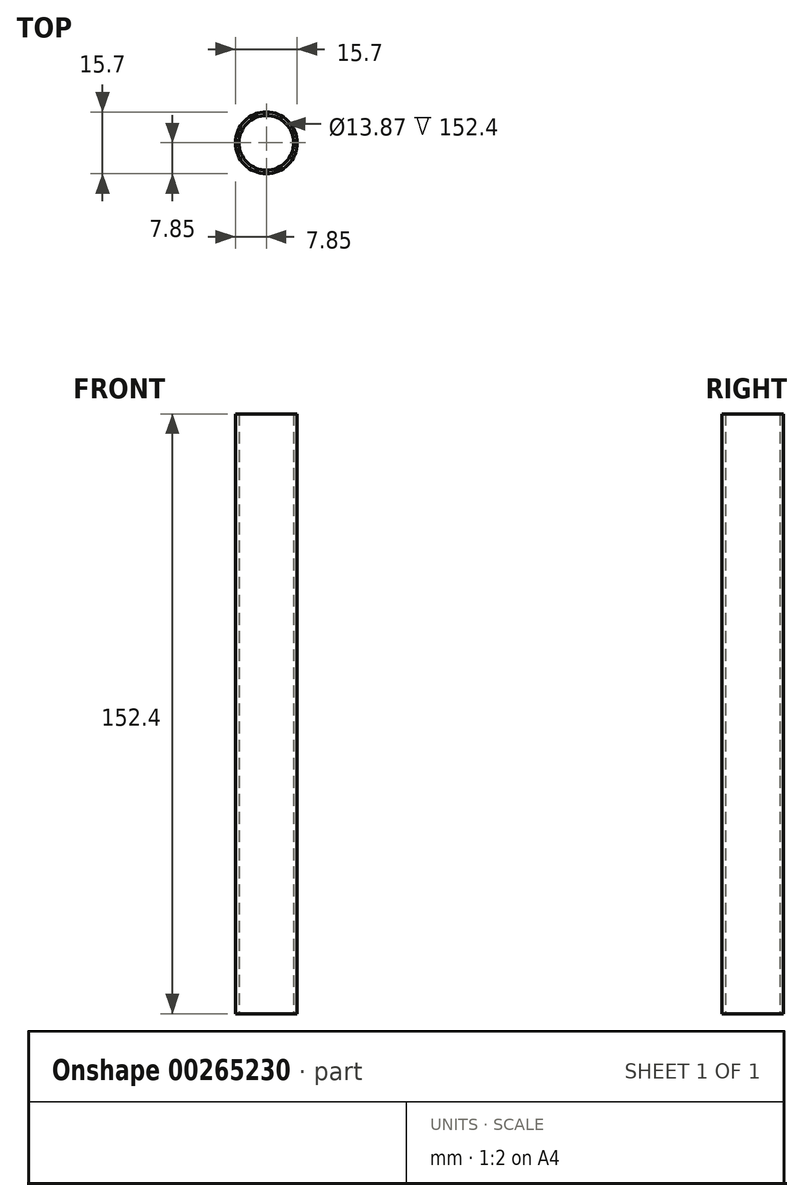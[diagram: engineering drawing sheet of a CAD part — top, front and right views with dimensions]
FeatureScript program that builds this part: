
annotation { "Feature Type Name" : "Feature", "Feature Type Description" : "" }
export const myFeature = defineFeature(function(context is Context, id is Id, definition is map)
    precondition{}
    {
        {
            var Q0;
            Q0=qCreatedBy(makeId("Top.planeOp"),FACE);
            var sketch = newSketch(context, id + "F0", { "sketchPlane" : qUnion([Q0])});
            skCircle(sketch, "E0", {"center": v(0, 0) * mm, "radius": 6.93 * mm});
            skCircle(sketch, "E1", {"center": v(0, 0) * mm, "radius": 7.85 * mm});
            skSolve(sketch);
        }
        {
            var Q0;
            Q0 = qSketchRegion(id + "F0", true);
            extrude(context, id + "F1", {"entities" : qUnion([Q0]), "depth" : 152.4 * mm});
        }
    });
